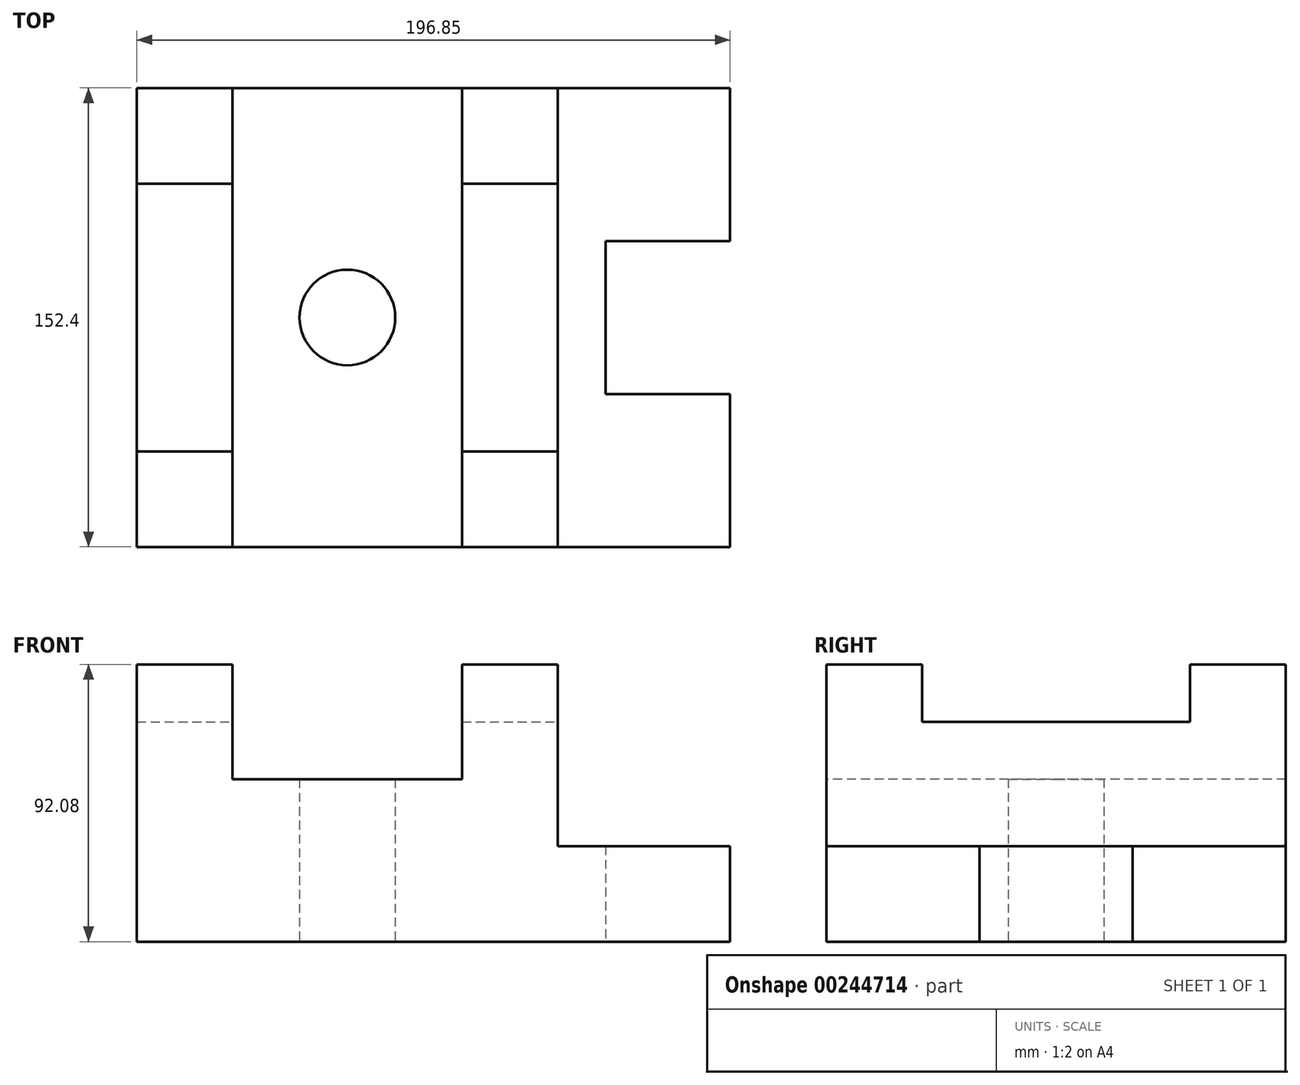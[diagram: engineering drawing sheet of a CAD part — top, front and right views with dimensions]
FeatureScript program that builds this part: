
annotation { "Feature Type Name" : "Feature", "Feature Type Description" : "" }
export const myFeature = defineFeature(function(context is Context, id is Id, definition is map)
    precondition{}
    {
        {
            var Q0;
            Q0=qCreatedBy(makeId("Top.planeOp"),FACE);
            var sketch = newSketch(context, id + "F0", { "sketchPlane" : qUnion([Q0])});
            skLineSegment(sketch, "E0", {"start": v(-74.34, -11.31) * mm, "end": v(52.66, -11.31) * mm});
            skLineSegment(sketch, "E1", {"start": v(52.66, 39.49) * mm, "end": v(11.39, 39.49) * mm});
            skLineSegment(sketch, "E2", {"start": v(52.66, 90.29) * mm, "end": v(11.39, 90.29) * mm});
            skLineSegment(sketch, "E3", {"start": v(52.66, 141.09) * mm, "end": v(-74.34, 141.09) * mm});
            skLineSegment(sketch, "E4", {"start": v(-4.49, 141.09) * mm, "end": v(-4.49, -11.31) * mm});
            skLineSegment(sketch, "E5", {"start": v(11.39, 90.29) * mm, "end": v(11.39, 39.49) * mm});
            skLineSegment(sketch, "E6", {"start": v(-36.24, 141.09) * mm, "end": v(-36.24, -11.31) * mm});
            skLineSegment(sketch, "E7", {"start": v(-36.24, 109.34) * mm, "end": v(-4.49, 109.34) * mm});
            skLineSegment(sketch, "E8", {"start": v(-36.24, 20.44) * mm, "end": v(-4.49, 20.44) * mm});
            skLineSegment(sketch, "E9", {"start": v(-74.34, -11.31) * mm, "end": v(-201.34, -11.31) * mm});
            skLineSegment(sketch, "E10", {"start": v(-74.34, 141.09) * mm, "end": v(-201.34, 141.09) * mm});
            skLineSegment(sketch, "E11", {"start": v(-144.19, 141.09) * mm, "end": v(-144.19, -11.31) * mm});
            skLineSegment(sketch, "E12", {"start": v(-112.44, 141.09) * mm, "end": v(-112.44, -11.31) * mm});
            skLineSegment(sketch, "E13", {"start": v(-144.19, 20.44) * mm, "end": v(-112.44, 20.44) * mm});
            skLineSegment(sketch, "E14", {"start": v(-144.19, 20.44) * mm, "end": v(-144.19, -11.31) * mm});
            skLineSegment(sketch, "E15", {"start": v(-112.44, 109.34) * mm, "end": v(-144.19, 109.34) * mm});
            skLineSegment(sketch, "E16", {"start": v(-201.34, 90.29) * mm, "end": v(-160.06, 90.29) * mm});
            skLineSegment(sketch, "E17", {"start": v(-201.34, 39.49) * mm, "end": v(-160.06, 39.49) * mm});
            skLineSegment(sketch, "E18", {"start": v(-160.06, 90.29) * mm, "end": v(-160.06, 39.49) * mm});
            skLineSegment(sketch, "E19", {"start": v(52.66, 141.09) * mm, "end": v(52.66, 90.29) * mm});
            skLineSegment(sketch, "E20", {"start": v(52.66, 39.49) * mm, "end": v(52.66, -11.31) * mm});
            skLineSegment(sketch, "E21", {"start": v(-201.34, 141.09) * mm, "end": v(-201.34, 90.29) * mm});
            skLineSegment(sketch, "E22", {"start": v(-201.34, 39.49) * mm, "end": v(-201.34, -11.31) * mm});
            skLineSegment(sketch, "E23", {"start": v(113.38, 115.92) * mm, "end": v(125.18, 115.92) * mm});
            skCircle(sketch, "E24", {"center": v(-74.34, 64.89) * mm, "radius": 15.88 * mm});
            skSolve(sketch);
        }
        {
            var Q0;
            {var subQ0=sQuery(id+"F0.wireOp",EDGE,"E14");Q0=makeQuery(id+"F0.imprint","IMPRINT",FACE,{"disambiguationData":[TD([[makeQuery(id+"F0.imprint","IMPRINT",EDGE,{"derivedFrom":subQ0}),-1.0]])]});}
            var Q1;
            {var subQ5=sQuery(id+"F0.wireOp",EDGE,"E15");Q1=makeQuery(id+"F0.imprint","IMPRINT",FACE,{"disambiguationData":[TD([[makeQuery(id+"F0.imprint","IMPRINT",EDGE,{"derivedFrom":subQ5}),-1.0]])]});}
            var Q2;
            {var subQ0=sQuery(id+"F0.wireOp",EDGE,"E13");Q2=makeQuery(id+"F0.imprint","IMPRINT",FACE,{"disambiguationData":[TD([[makeQuery(id+"F0.imprint","IMPRINT",EDGE,{"derivedFrom":subQ0}),1.0]])]});}
            var Q3;
            {var subQ4=sQuery(id+"F0.wireOp",EDGE,"E13");Q3=makeQuery(id+"F0.imprint","IMPRINT",FACE,{"disambiguationData":[TD([[makeQuery(id+"F0.imprint","IMPRINT",EDGE,{"derivedFrom":subQ4}),-1.0]])]});}
            var Q4;
            {var subQ0=sQuery(id+"F0.wireOp",EDGE,"E10");var subQ3=sQuery(id+"F0.wireOp",EDGE,"E12");var subQ4=makeQuery(id+"F0.imprint","INTERSECT",VERTEX,{"derivedFrom":[subQ0,subQ3]});Q4=makeQuery(id+"F0.imprint","IMPRINT",FACE,{"disambiguationData":[TD([[makeQuery(id+"F0.imprint","IMPRINT",EDGE,{"disambiguationData":[TD([[subQ4,-1.0]])],"derivedFrom":subQ3}),1.0]])]});}
            var Q5;
            {var subQ5=sQuery(id+"F0.wireOp",EDGE,"E3");var subQ8=sQuery(id+"F0.wireOp",EDGE,"E6");var subQ9=makeQuery(id+"F0.imprint","INTERSECT",VERTEX,{"derivedFrom":[subQ5,subQ8]});Q5=makeQuery(id+"F0.imprint","IMPRINT",FACE,{"disambiguationData":[TD([[makeQuery(id+"F0.imprint","IMPRINT",EDGE,{"disambiguationData":[TD([[subQ9,-1.0]])],"derivedFrom":subQ8}),-1.0]])]});}
            var Q6;
            {var subQ0=sQuery(id+"F0.wireOp",EDGE,"E7");Q6=makeQuery(id+"F0.imprint","IMPRINT",FACE,{"disambiguationData":[TD([[makeQuery(id+"F0.imprint","IMPRINT",EDGE,{"derivedFrom":subQ0}),-1.0]])]});}
            var Q7;
            Q7=makeQuery(id+"F0.imprint","IMPRINT",FACE,{"disambiguationData":[TD([[makeQuery(id+"F0.imprint","IMPRINT",EDGE,{"derivedFrom":sQuery(id+"F0.wireOp",EDGE,"E1")}),1.0]])]});
            var Q8;
            {var subQ5=sQuery(id+"F0.wireOp",EDGE,"E8");Q8=makeQuery(id+"F0.imprint","IMPRINT",FACE,{"disambiguationData":[TD([[makeQuery(id+"F0.imprint","IMPRINT",EDGE,{"derivedFrom":subQ5}),-1.0]])]});}
            var Q9;
            {var subQ5=sQuery(id+"F0.wireOp",EDGE,"E7");Q9=makeQuery(id+"F0.imprint","IMPRINT",FACE,{"disambiguationData":[TD([[makeQuery(id+"F0.imprint","IMPRINT",EDGE,{"derivedFrom":subQ5}),1.0]])]});}
            extrude(context, id + "F1", {"entities" : qUnion([Q0, Q1, Q2, Q3, Q4, Q5, Q6, Q7, Q8, Q9]), "depth" : 92.07 * mm});
        }
        {
            var Q0;
            Q0=makeQuery(id+"F1.opExtrude","SWEPT_FACE",FACE,{"disambiguationData":[OSD([sQuery(id+"F0.wireOp",EDGE,"E0"),sQuery(id+"F0.wireOp",EDGE,"E9")])]});
            var sketch = newSketch(context, id + "F2", { "sketchPlane" : qUnion([Q0])});
            skLineSegment(sketch, "E25", {"start": v(-201.34, 31.75) * mm, "end": v(-144.19, 31.75) * mm});
            skLineSegment(sketch, "E26", {"start": v(-144.19, 31.75) * mm, "end": v(-144.19, 92.08) * mm});
            skLineSegment(sketch, "E27", {"start": v(-144.19, 92.08) * mm, "end": v(-112.44, 92.08) * mm});
            skLineSegment(sketch, "E28", {"start": v(-112.44, 92.08) * mm, "end": v(-112.44, 53.97) * mm});
            skLineSegment(sketch, "E29", {"start": v(-112.44, 53.97) * mm, "end": v(-36.24, 53.98) * mm});
            skLineSegment(sketch, "E30", {"start": v(-36.24, 53.98) * mm, "end": v(-36.24, 92.08) * mm});
            skLineSegment(sketch, "E31", {"start": v(-36.24, 92.08) * mm, "end": v(-4.49, 92.08) * mm});
            skLineSegment(sketch, "E32", {"start": v(-4.49, 92.08) * mm, "end": v(-4.49, 31.75) * mm});
            skLineSegment(sketch, "E33", {"start": v(-4.49, 31.75) * mm, "end": v(52.66, 31.75) * mm});
            skSolve(sketch);
        }
        {
            var Q0;
            {var subQ0=sQuery(id+"F2.wireOp",EDGE,"E25");Q0=makeQuery(id+"F2.imprint","IMPRINT",FACE,{"disambiguationData":[TD([[makeQuery(id+"F2.imprint","IMPRINT",EDGE,{"derivedFrom":subQ0}),1.0]])]});}
            var Q1;
            {var subQ0=sQuery(id+"F2.wireOp",EDGE,"E28");Q1=makeQuery(id+"F2.imprint","IMPRINT",FACE,{"disambiguationData":[TD([[makeQuery(id+"F2.imprint","IMPRINT",EDGE,{"derivedFrom":subQ0}),1.0]])]});}
            var Q2;
            {var subQ0=sQuery(id+"F2.wireOp",EDGE,"E32");Q2=makeQuery(id+"F2.imprint","IMPRINT",FACE,{"disambiguationData":[TD([[makeQuery(id+"F2.imprint","IMPRINT",EDGE,{"derivedFrom":subQ0}),1.0]])]});}
            extrude(context, id + "F3", {"entities" : qUnion([Q0, Q1, Q2]), "operationType" : NewBodyOperationType.REMOVE, "endBound" : BoundingType.THROUGH_ALL, "oppositeDirection" : true, "depth" : 25.4 * mm});
        }
        {
            var Q0;
            Q0=makeQuery(id+"F3.boolean.opBoolean","COPY",FACE,{"derivedFrom":makeQuery(id+"F3.opExtrude","SWEPT_FACE",FACE,{"disambiguationData":[OSD([sQuery(id+"F2.wireOp",EDGE,"E32")])]})});
            var sketch = newSketch(context, id + "F4", { "sketchPlane" : qUnion([Q0])});
            skLineSegment(sketch, "E34", {"start": v(20.44, 92.08) * mm, "end": v(20.44, 73.02) * mm});
            skLineSegment(sketch, "E35", {"start": v(20.44, 73.02) * mm, "end": v(109.34, 73.03) * mm});
            skLineSegment(sketch, "E36", {"start": v(109.34, 73.03) * mm, "end": v(109.34, 92.08) * mm});
            skSolve(sketch);
        }
        {
            var Q0;
            {var subQ0=sQuery(id+"F4.wireOp",EDGE,"E34");Q0=makeQuery(id+"F4.imprint","IMPRINT",FACE,{"disambiguationData":[TD([[makeQuery(id+"F4.imprint","IMPRINT",EDGE,{"derivedFrom":subQ0}),1.0]])]});}
            extrude(context, id + "F5", {"entities" : qUnion([Q0]), "operationType" : NewBodyOperationType.REMOVE, "endBound" : BoundingType.THROUGH_ALL, "oppositeDirection" : true, "depth" : 25.4 * mm});
        }
    });
